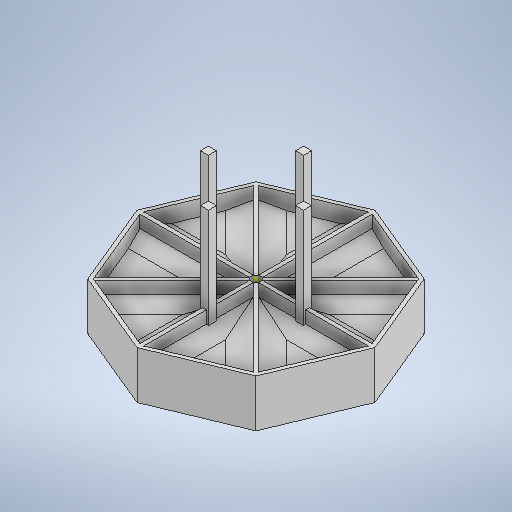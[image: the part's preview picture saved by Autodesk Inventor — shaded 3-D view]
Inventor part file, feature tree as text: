
AUTODESK INVENTOR PART (.ipt)
format: ipt  version: 2025 (Build 290162000, 162)  size: 497,152 bytes
history: native  units: mm
features: sketch x14, extrude x9, chamfer x8, projected_geometry x2
ambient origin geometry x8: Origin, YZ Plane, XZ Plane, XY Plane, X Axis, Y Axis, Z Axis, Center Point
bodies: Body1 (feature_tree)
feature tree (33):
  extrude  "Wyciągnięcie proste2"  Depth=300.0mm
  sketch  "Szkic4"
  extrude  "Wyciągnięcie proste3"  Depth=50.0mm TaperAngle=0.0deg
  sketch  "Szkic6"
  extrude  "Wyciągnięcie proste4"  Depth=290.0mm
  extrude  "Wyciągnięcie proste5"  Depth=30.0mm TaperAngle=0.0deg
  extrude  "Wyciągnięcie proste6"  Depth=5.0mm
  sketch  "Szkic10"
  extrude  "Wyciągnięcie proste7"  Depth=5.0mm
  extrude  "Wyciągnięcie proste14"  Depth=5.0mm
  sketch  "Szkic20"
  sketch  "Szkic21"
  extrude  "Wyciągnięcie proste15"  Depth=5.0mm
  chamfer  "Faza1"  Distance=30.0mm
  extrude  "Wyciągnięcie proste16"  Depth=12.0mm
  chamfer  "Faza2"  Distance=12.0mm
  chamfer  "Faza3"  Distance=75.0mm
  chamfer  "Faza4"  Distance=19.0mm
  chamfer  "Faza5"  Distance=10.0mm
  chamfer  "Faza6"  Distance=110.0mm
  chamfer  "Faza7"  Distance=57.5mm
  chamfer  "Faza8"  Distance=10.0mm
  sketch  "Szkic3"
  sketch  "Szkic5"
  sketch  "Szkic7"
  sketch  "Szkic8"
  sketch  "Szkic9"
  sketch  "Szkic11"
  projected_geometry  "Pętla rzutowana1"
  projected_geometry  "Pętla rzutowana2"
  sketch  "Szkic19"
  sketch  "Szkic22"
  sketch  "Szkic23"
